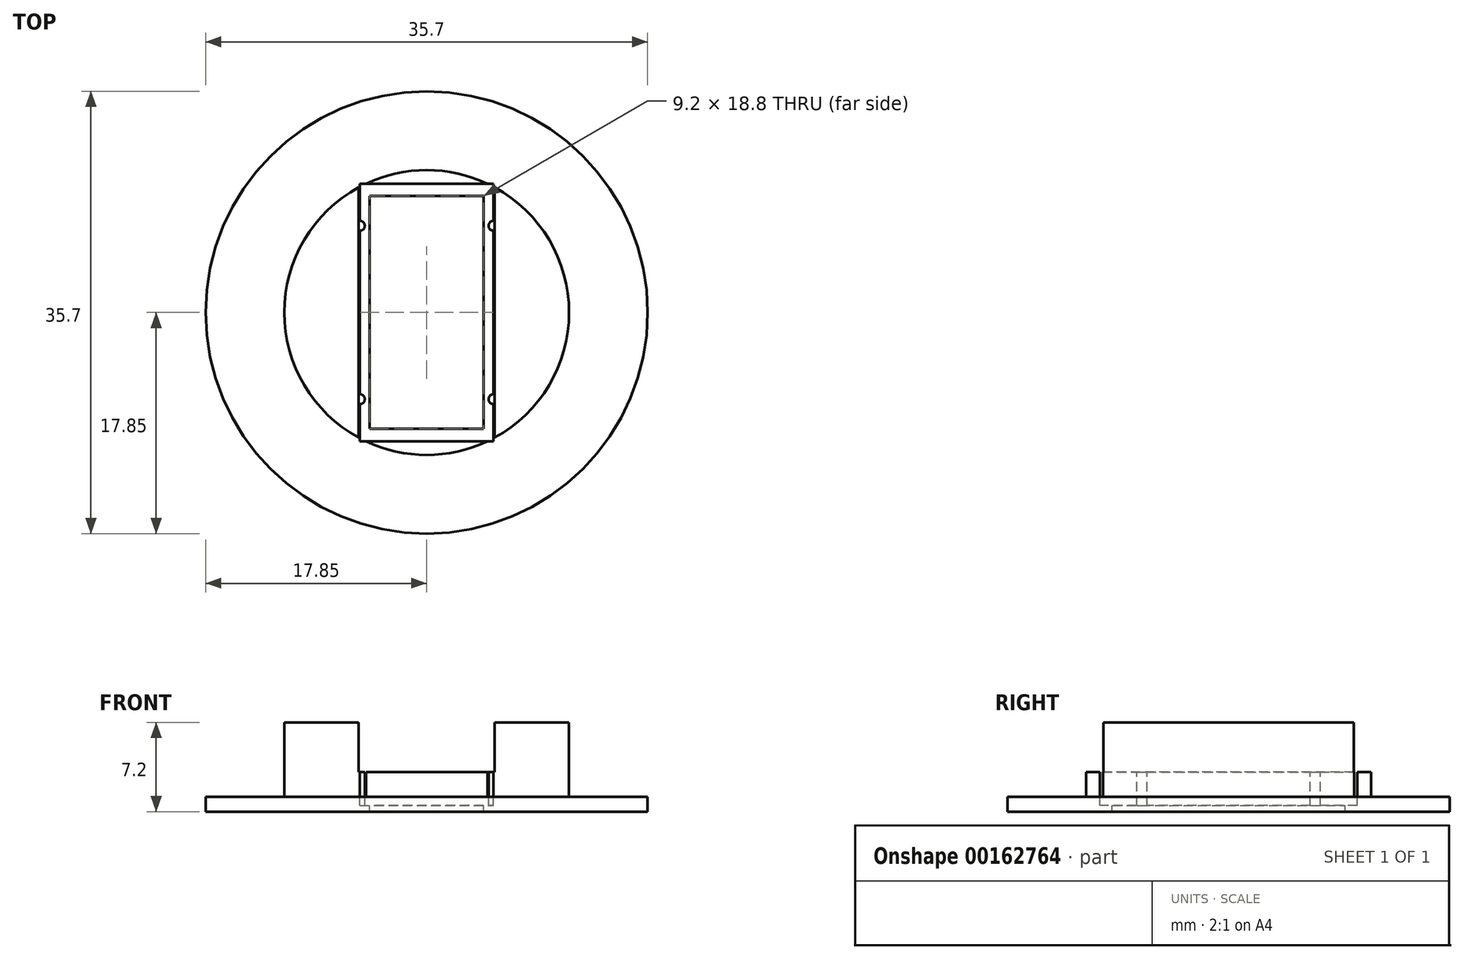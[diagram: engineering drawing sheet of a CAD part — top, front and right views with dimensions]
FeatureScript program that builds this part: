
annotation { "Feature Type Name" : "Feature", "Feature Type Description" : "" }
export const myFeature = defineFeature(function(context is Context, id is Id, definition is map)
    precondition{}
    {
        {
            var Q0;
            Q0=qCreatedBy(makeId("Top.planeOp"),FACE);
            var sketch = newSketch(context, id + "F0", { "sketchPlane" : qUnion([Q0])});
            skCircle(sketch, "E0", {"center": v(0, 0) * mm, "radius": 17.85 * mm});
            skSolve(sketch);
        }
        {
            var Q0;
            Q0=qSketchRegion(id+"F0",true);
            extrude(context, id + "F1", {"entities" : qUnion([Q0]), "depth" : 1.2 * mm});
        }
        {
            var Q0;
            Q0=makeQuery(id+"F1.opExtrude","CAP_FACE",FACE,{"disambiguationData":[OSD([sQuery(id+"F0.wireOp",EDGE,"E0")])],"isStart":false});
            var sketch = newSketch(context, id + "F2", { "sketchPlane" : qUnion([Q0])});
            skCircle(sketch, "E1", {"center": v(0, 0) * mm, "radius": 11.5 * mm});
            skSolve(sketch);
        }
        {
            var Q0;
            Q0=qSketchRegion(id+"F2",true);
            extrude(context, id + "F3", {"entities" : qUnion([Q0]), "operationType" : NewBodyOperationType.ADD, "depth" : 6 * mm});
        }
        {
            var Q0;
            Q0=makeQuery(id+"F3.opExtrude","CAP_FACE",FACE,{"disambiguationData":[OSD([sQuery(id+"F2.wireOp",EDGE,"E1")])],"isStart":false});
            var sketch = newSketch(context, id + "F4", { "sketchPlane" : qUnion([Q0])});
            skLineSegment(sketch, "E2.bottom", {"start": v(-4.6, 9.4) * mm, "end": v(4.6, 9.4) * mm});
            skLineSegment(sketch, "E2.top", {"start": v(-4.6, -9.4) * mm, "end": v(4.6, -9.4) * mm});
            skLineSegment(sketch, "E2.left", {"start": v(-4.6, 9.4) * mm, "end": v(-4.6, -9.4) * mm});
            skLineSegment(sketch, "E2.right", {"start": v(4.6, 9.4) * mm, "end": v(4.6, -9.4) * mm});
            skSolve(sketch);
        }
        {
            var Q0;
            Q0=qSketchRegion(id+"F4",true);
            extrude(context, id + "F5", {"entities" : qUnion([Q0]), "operationType" : NewBodyOperationType.REMOVE, "endBound" : BoundingType.THROUGH_ALL, "oppositeDirection" : true, "depth" : 25 * mm});
        }
        {
            var Q0;
            Q0=makeQuery(id+"F3.opExtrude","CAP_FACE",FACE,{"disambiguationData":[OSD([sQuery(id+"F2.wireOp",EDGE,"E1")])],"isStart":false});
            var sketch = newSketch(context, id + "F6", { "sketchPlane" : qUnion([Q0])});
            skLineSegment(sketch, "E3.bottom", {"start": v(-5.4, 10.4) * mm, "end": v(5.4, 10.4) * mm});
            skLineSegment(sketch, "E3.top", {"start": v(-5.4, -10.4) * mm, "end": v(5.4, -10.4) * mm});
            skLineSegment(sketch, "E3.left", {"start": v(-5.4, 10.4) * mm, "end": v(-5.4, 7.4) * mm});
            skLineSegment(sketch, "E3.right", {"start": v(5.4, 10.4) * mm, "end": v(5.4, 7.4) * mm});
            skArc(sketch, "E4", {"start": v(5.4, 7.4) * mm, "mid": v(5, 7) * mm, "end": v(5.4, 6.6) * mm});
            skArc(sketch, "E5", {"start": v(5.4, -6.6) * mm, "mid": v(5, -7) * mm, "end": v(5.4, -7.4) * mm});
            skArc(sketch, "E6", {"start": v(-5.4, 6.6) * mm, "mid": v(-5, 7) * mm, "end": v(-5.4, 7.4) * mm});
            skArc(sketch, "E7", {"start": v(-5.4, -7.4) * mm, "mid": v(-5, -7) * mm, "end": v(-5.4, -6.6) * mm});
            skLineSegment(sketch, "E8.trimOffspring", {"start": v(5.4, 6.6) * mm, "end": v(5.4, -6.6) * mm});
            skLineSegment(sketch, "E9.trimOffspring", {"start": v(-5.4, 6.6) * mm, "end": v(-5.4, -6.6) * mm});
            skLineSegment(sketch, "E10.trimOffspring", {"start": v(-5.4, -7.4) * mm, "end": v(-5.4, -10.4) * mm});
            skLineSegment(sketch, "E11.trimOffspring", {"start": v(5.4, -7.4) * mm, "end": v(5.4, -10.4) * mm});
            skSolve(sketch);
        }
        {
            var Q0;
            Q0=qSketchRegion(id+"F6",true);
            extrude(context, id + "F7", {"entities" : qUnion([Q0]), "operationType" : NewBodyOperationType.REMOVE, "oppositeDirection" : true, "depth" : 6.7 * mm});
        }
        {
            var Q0;
            {var subQ0=sQuery(id+"F2.wireOp",EDGE,"E1");Q0=makeQuery(id+"F7.boolean.opBoolean","SPLIT",FACE,{"disambiguationData":[TD([makeQuery(id+"F7.opExtrude","SWEPT_FACE",FACE,{"disambiguationData":[OSD([sQuery(id+"F6.wireOp",EDGE,"E3.right")])]})])],"derivedFrom":makeQuery(id+"F3.opExtrude","CAP_FACE",FACE,{"disambiguationData":[OSD([subQ0])],"isStart":false})});}
            var sketch = newSketch(context, id + "F8", { "sketchPlane" : qUnion([Q0])});
            skLineSegment(sketch, "E12.bottom", {"start": v(-5.5, 12.5) * mm, "end": v(5.5, 12.5) * mm});
            skLineSegment(sketch, "E12.top", {"start": v(-5.5, -12.5) * mm, "end": v(5.5, -12.5) * mm});
            skLineSegment(sketch, "E12.left", {"start": v(-5.5, 12.5) * mm, "end": v(-5.5, -12.5) * mm});
            skLineSegment(sketch, "E12.right", {"start": v(5.5, 12.5) * mm, "end": v(5.5, -12.5) * mm});
            skSolve(sketch);
        }
        {
            var Q0;
            Q0 = qSketchRegion(id + "F8", true);
            extrude(context, id + "F9", {"entities" : qUnion([Q0]), "operationType" : NewBodyOperationType.REMOVE, "oppositeDirection" : true, "depth" : 4 * mm});
        }
    });
